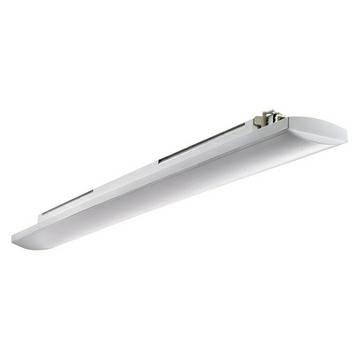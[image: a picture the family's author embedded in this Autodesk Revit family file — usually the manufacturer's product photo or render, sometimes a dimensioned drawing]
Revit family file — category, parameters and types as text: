
# Revit family: Lighting-Industrial-GEWISS-SMART[3]e-WATERTIGHT-LED_OPAL_800mm
name_source: partatom
category: Apparecchi per illuminazione
units: mm (PartAtom-declared; Revit-internal decimal feet)

## family parameters
Condiviso = No
Host = Superficie
Punto di calcolo locali = Sì
Quota connettore circolare = Usa diametro
Sorgente d'illuminazione = No
Taglio con vuoti quando caricato = No
Tipo di parte = Normale

## types (2) — shared parameters
Application = Internal
Body = Polycarbonate
Carico apparente = 27 VA
Catalogue = LIGHTING
Classification: = -
Color Rendering Index = CRI>80
Colour = Grey RAL 7035
Colour : = RAL7035 colored PC paste
Commenti sul wattaggio = 27W
Context = Lighting of warehouses, indoor parking and industrial production rooms
Control System = Stand Alone - On / Off
Control System : = ON / OFF
DIN 18032-3 certification = Not available
Device with reduced surface temperature = Yes
Driver = Included
Driver Box = Built-in
Driver failure rate = F10 = 90.000 h a Tq 25°C/F10= 50.000 h a Tq 40°C
Eletrical and lighting features = -
External screw = -
Fixing = Stainless steel support
Ganci = GEWISS  - ALLUMINIO
Gasket = CNC deposited sealant
General information = -
Glow Wire Test : = 850 °C
IDF = 76292b3c-4f10-4a74-a7ee-aa3a8e861517
IDT = c14e9783-cfcd-4d50-ad03-d02503739214
IP degree = IP66/IP69
IPEA = -
Immagine tipo = GWS3118P.jpg
Installationa and maintenance = -
Insulation class = II
LED Maintenance = Not available
Lampada = LED
Lifetime = L80B20(Tq25°C)=90.000h - L80B20(Tq40°C)=50.000h
Locking Hook = -
Luminaire = LED fixture for general lighting
Lunghezza Lampada = 800 mm  [stored 2.62467 ft]
Materials = -
Maximum surface exposed to the wind : = -
Mouting and installation = Ceiling - Wallmounting - Suspension
Operating temperature : = -25 +40 °C
Optic = Wide opal
Optic : = Integrated in the screen
Optic Maintenance = Not available
Optic and illuminating features = -
Overvoltage protection = DM 1KV / CM 2KV
Photobiological Risk Class = -
Produttore = GEWISS S.p.A.
Prospetto di default = 1219 mm
Rated frequency (Hz) = 50/60 Hz
Schermo. = Gewiss - Led Acceso
Shield type = UV stabilised polycarbonate
Shock resistance = IK08
Stampa 1_100 = Sì
Stampa 1_200 = No
Standard Deviation Colour Matching = SDCM = 3
Standard- = EN60598-1; IEC 62778; IEC62471
Standards and approvals = -
Stocking temperature = -25 +80 °C
Struttura = GEWISS - SMART 3 - GRIGIO
Supply voltage = 220 - 240 V
Technical sheet = https://www.gewiss.com
Tilt- = With fixing bracket
Type of light source = LED - Not replaceable
URL = https://www.gewiss.com
Unified Glare Rating = UGR < 25 (4H/8H)
Unique digital code (Datamatrix) = Datamatrix
Version file RFA = 21.4
Warranty = 5 years
Wiring = With GW connect watertight connector
Wiring : = Stand alone

## per-type parameters (varying)
| type | Descrizione | Modello |
| GWS3120EP840 - SMART3e 800 ON/OFF OPAL CRI80 4000K | SMART3e 800 ON/OFF OPAL CRI80 4000K | GWS3120EP840 |
| GWS3120EP857 - SMART3e 800 ON/OFF OPAL CRI80 5700K | SMART3e 800 ON/OFF OPAL CRI80 5700K | GWS3120EP857 |

note: [stored X ft] marks values corroborated as IEEE doubles in the binary element streams (Revit-internal decimal feet)
